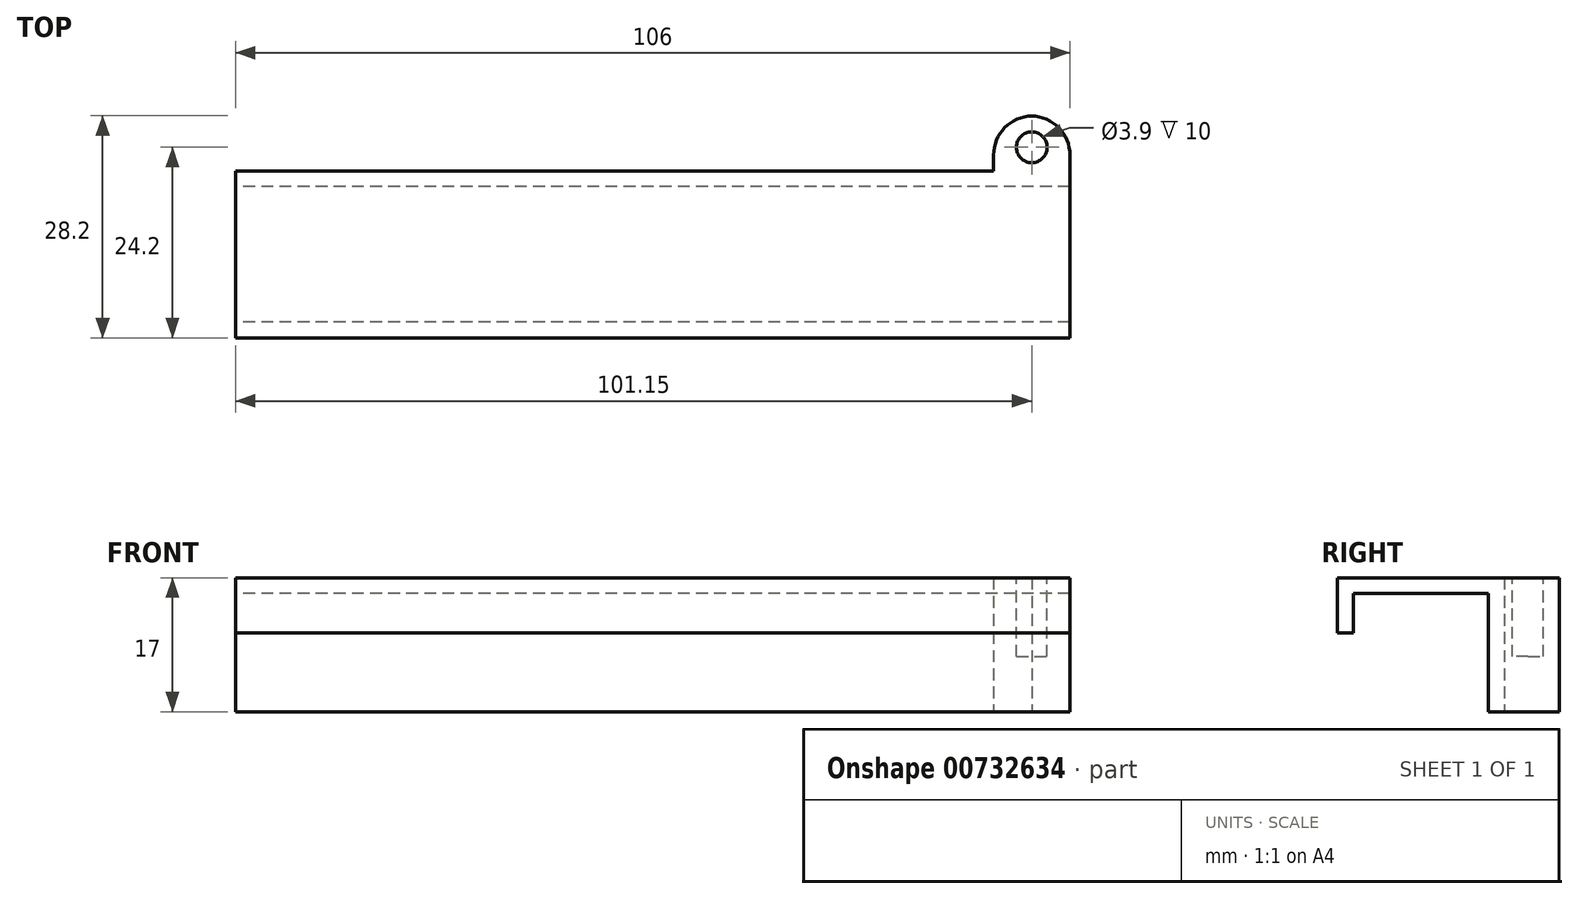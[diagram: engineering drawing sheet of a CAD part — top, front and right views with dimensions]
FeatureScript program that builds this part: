
annotation { "Feature Type Name" : "Feature", "Feature Type Description" : "" }
export const myFeature = defineFeature(function(context is Context, id is Id, definition is map)
    precondition{}
    {
        {
            var Q0;
            Q0=qCreatedBy(makeId("Right.planeOp"),FACE);
            var sketch = newSketch(context, id + "F0", { "sketchPlane" : qUnion([Q0])});
            skLineSegment(sketch, "E0", {"start": v(0, 0) * mm, "end": v(-17.2, 0) * mm});
            skLineSegment(sketch, "E1", {"start": v(-17.2, 0) * mm, "end": v(-17.2, -5) * mm});
            skLineSegment(sketch, "E2", {"start": v(0, 0) * mm, "end": v(0, -15) * mm});
            skLineSegment(sketch, "E3.0", {"start": v(-19.2, 2) * mm, "end": v(-19.2, -5) * mm});
            skLineSegment(sketch, "E3.1", {"start": v(2, 2) * mm, "end": v(-19.2, 2) * mm});
            skLineSegment(sketch, "E3.2", {"start": v(2, 2) * mm, "end": v(2, -15) * mm});
            skLineSegment(sketch, "E4", {"start": v(-17.2, -5) * mm, "end": v(-19.2, -5) * mm});
            skLineSegment(sketch, "E5", {"start": v(0, -15) * mm, "end": v(2, -15) * mm});
            skSolve(sketch);
        }
        {
            var Q0;
            Q0=makeQuery(id+"F0.imprint","IMPRINT",FACE,{"disambiguationData":[TD([[makeQuery(id+"F0.imprint","IMPRINT",EDGE,{"derivedFrom":sQuery(id+"F0.wireOp",EDGE,"E0")}),-1.0]])]});
            extrude(context, id + "F1", {"entities" : qUnion([Q0]), "endBound" : BoundingType.SYMMETRIC, "depth" : 106 * mm, "offsetDistance" : 25 * mm});
        }
        {
            var Q0;
            Q0=makeQuery(id+"F1.opExtrude","SWEPT_FACE",FACE,{"disambiguationData":[OSD([sQuery(id+"F0.wireOp",EDGE,"E3.2")])]});
            var sketch = newSketch(context, id + "F2", { "sketchPlane" : qUnion([Q0])});
            skLineSegment(sketch, "E6.bottom", {"start": v(-53, 2) * mm, "end": v(-43.3, 2) * mm});
            skLineSegment(sketch, "E6.top", {"start": v(-53, -15) * mm, "end": v(-43.3, -15) * mm});
            skLineSegment(sketch, "E6.left", {"start": v(-53, 2) * mm, "end": v(-53, -15) * mm});
            skLineSegment(sketch, "E6.right", {"start": v(-43.3, 2) * mm, "end": v(-43.3, -15) * mm});
            skSolve(sketch);
        }
        {
            var Q0;
            Q0=makeQuery(id+"F2.imprint","IMPRINT",FACE,{"disambiguationData":[TD([[makeQuery(id+"F2.imprint","IMPRINT",EDGE,{"derivedFrom":sQuery(id+"F2.wireOp",EDGE,"E6.bottom")}),-1.0]])]});
            extrude(context, id + "F3", {"entities" : qUnion([Q0]), "operationType" : NewBodyOperationType.ADD, "depth" : 7 * mm, "offsetDistance" : 25 * mm});
        }
        {
            var Q0;
            Q0=makeQuery(id+"F3.boolean.opBoolean","MERGE",FACE,{"derivedFrom":[makeQuery(id+"F1.opExtrude","SWEPT_FACE",FACE,{"disambiguationData":[OSD([sQuery(id+"F0.wireOp",EDGE,"E3.1")])]}),makeQuery(id+"F3.opExtrude","SWEPT_FACE",FACE,{"disambiguationData":[OSD([sQuery(id+"F2.wireOp",EDGE,"E6.bottom")])]})]});
            var sketch = newSketch(context, id + "F4", { "sketchPlane" : qUnion([Q0])});
            skLineSegment(sketch, "E7", {"start": v(43.3, 2) * mm, "end": v(53, 2) * mm, "construction": true});
            skCircle(sketch, "E8", {"center": v(48.15, 5) * mm, "radius": 1.95 * mm});
            skSolve(sketch);
        }
        {
            var Q0;
            Q0=makeQuery(id+"F4.imprint","IMPRINT",FACE,{"disambiguationData":[TD([[makeQuery(id+"F4.imprint","IMPRINT",EDGE,{"derivedFrom":sQuery(id+"F4.wireOp",EDGE,"E8")}),1.0]])]});
            extrude(context, id + "F5", {"entities" : qUnion([Q0]), "operationType" : NewBodyOperationType.REMOVE, "oppositeDirection" : true, "depth" : 25 * mm, "offsetDistance" : 25 * mm});
        }
        {
            var Q0;
            Q0=makeQuery(id+"F3.opExtrude","CAP_EDGE",EDGE,{"disambiguationData":[OSD([sQuery(id+"F2.wireOp",EDGE,"E6.left")])],"isStart":false});
            var Q1;
            Q1=makeQuery(id+"F3.opExtrude","CAP_EDGE",EDGE,{"disambiguationData":[OSD([sQuery(id+"F2.wireOp",EDGE,"E6.right")])],"isStart":false});
            fillet(context, id + "F6", {"entities" : qUnion([Q0, Q1]), "radius" : 5 * mm, "tangentPropagation" : true, "allowEdgeOverflow" : false});
        }
        {
            var Q0;
            {var subQ0=sQuery(id+"F2.wireOp",EDGE,"E6.top");Q0=makeQuery(id+"FJF3MdRUaZqlzXo_1.1.F3.boolean.opBoolean","MERGE",FACE,{"derivedFrom":[makeQuery(id+"F3.boolean.opBoolean","MERGE",FACE,{"derivedFrom":[makeQuery(id+"F1.opExtrude","SWEPT_FACE",FACE,{"disambiguationData":[OSD([sQuery(id+"F0.wireOp",EDGE,"E5")])]}),makeQuery(id+"F3.opExtrude","SWEPT_FACE",FACE,{"disambiguationData":[OSD([subQ0])]})]}),makeQuery(id+"FJF3MdRUaZqlzXo_1.1.F3.opExtrude","SWEPT_FACE",FACE,{"disambiguationData":[OSD([subQ0])]})]});}
            var sketch = newSketch(context, id + "F7", { "sketchPlane" : qUnion([Q0])});
            skSolve(sketch);
        }
        {
            var Q0;
            Q0=makeQuery(id+"F7.imprint","IMPRINT",FACE,{"disambiguationData":[TD([[makeQuery(id+"F7.imprint","IMPRINT",EDGE,{"derivedFrom":makeQuery(id+"F5.boolean.opBoolean","INTERSECT",EDGE,{"derivedFrom":[makeQuery(id+"F3.boolean.opBoolean","MERGE",FACE,{"derivedFrom":[makeQuery(id+"F1.opExtrude","SWEPT_FACE",FACE,{"disambiguationData":[OSD([sQuery(id+"F0.wireOp",EDGE,"E5")])]}),makeQuery(id+"F3.opExtrude","SWEPT_FACE",FACE,{"disambiguationData":[OSD([sQuery(id+"F2.wireOp",EDGE,"E6.top")])]})]}),makeQuery(id+"F5.opExtrude","SWEPT_FACE",FACE,{"disambiguationData":[OSD([sQuery(id+"F4.wireOp",EDGE,"E8")])]})]})}),-1.0]])]});
            extrude(context, id + "F8", {"entities" : qUnion([Q0]), "operationType" : NewBodyOperationType.ADD, "oppositeDirection" : true, "depth" : 7 * mm, "offsetDistance" : 25 * mm});
        }
    });
